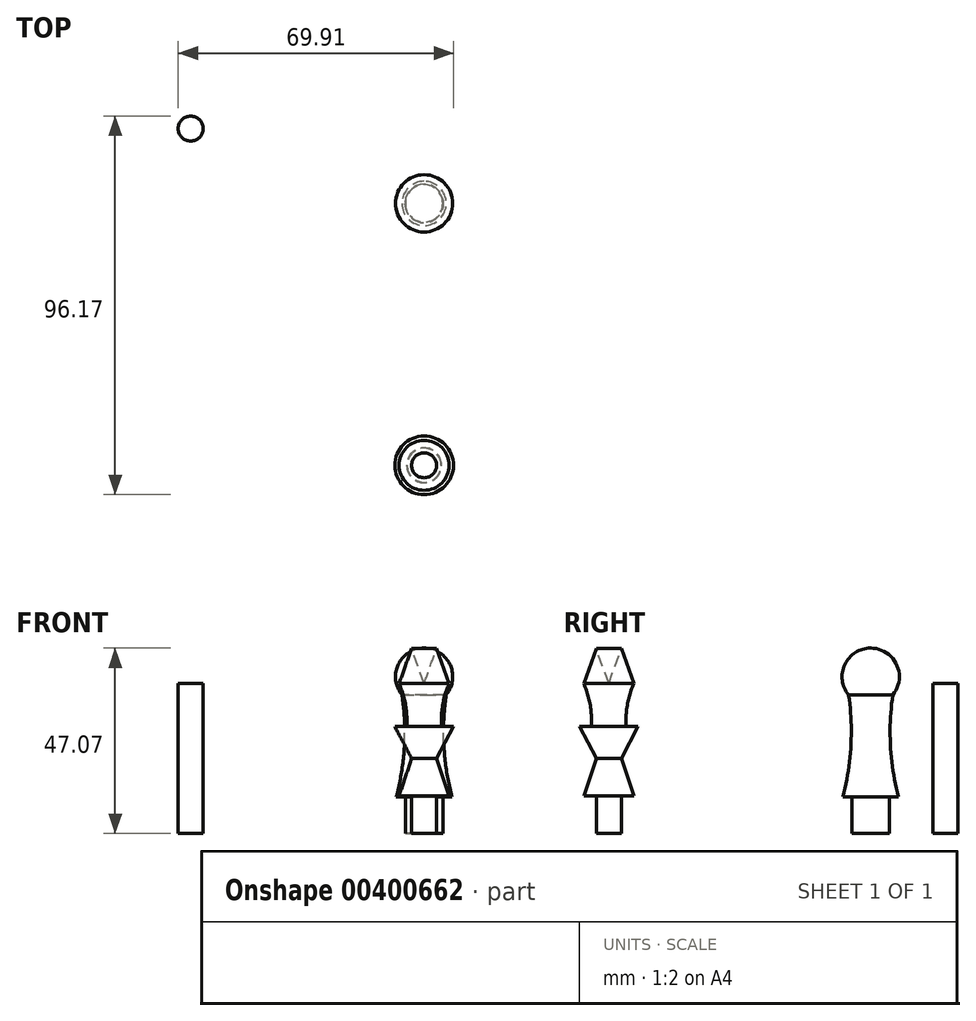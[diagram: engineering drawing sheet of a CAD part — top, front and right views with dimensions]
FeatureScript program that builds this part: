
annotation { "Feature Type Name" : "Feature", "Feature Type Description" : "" }
export const myFeature = defineFeature(function(context is Context, id is Id, definition is map)
    precondition{}
    {
        {
            var Q0;
            Q0=qCreatedBy(makeId("Top.planeOp"),FACE);
            var sketch = newSketch(context, id + "F0", { "sketchPlane" : qUnion([Q0])});
            skCircle(sketch, "E0", {"center": v(-59.29, 19) * mm, "radius": 3.18 * mm});
            skSolve(sketch);
        }
        {
            var Q0;
            Q0=makeQuery(id+"F0.imprint","IMPRINT",FACE,{"disambiguationData":[TD([[makeQuery(id+"F0.imprint","IMPRINT",EDGE,{"derivedFrom":sQuery(id+"F0.wireOp",EDGE,"E0")}),1.0]])]});
            extrude(context, id + "F1", {"entities" : qUnion([Q0]), "depth" : 38.1 * mm});
        }
        {
            var Q0;
            Q0=qCreatedBy(makeId("Right.planeOp"),FACE);
            var sketch = newSketch(context, id + "F2", { "sketchPlane" : qUnion([Q0])});
            skLineSegment(sketch, "E1", {"start": v(0, 0) * mm, "end": v(0, 47.07) * mm});
            skArc(sketch, "E2", {"start": v(5.62, 35.19) * mm, "mid": v(6.57, 42.9) * mm, "end": v(0, 47.07) * mm});
            skLineSegment(sketch, "E3", {"start": v(4.76, 0) * mm, "end": v(0, 0) * mm});
            skLineSegment(sketch, "E4", {"start": v(4.76, 0) * mm, "end": v(4.76, 9.26) * mm});
            skLineSegment(sketch, "E5", {"start": v(4.76, 9.26) * mm, "end": v(7.08, 9.26) * mm});
            skArc(sketch, "E6", {"start": v(5.62, 35.19) * mm, "mid": v(5.03, 22.15) * mm, "end": v(7.08, 9.26) * mm});
            skSolve(sketch);
        }
        {
            var Q0;
            Q0 = qSketchRegion(id + "F2", true);
            var Q1;
            Q1=sQuery(id+"F2.wireOp",EDGE,"E1");
            revolve(context, id + "F3", {"entities" : qUnion([Q0]), "axis" : qUnion([Q1]), "revolveType" : RevolveType.FULL});
        }
        {
            var Q0;
            Q0=qCreatedBy(makeId("Right.planeOp"),FACE);
            var sketch = newSketch(context, id + "F4", { "sketchPlane" : qUnion([Q0])});
            skLineSegment(sketch, "E7", {"start": v(-66.55, 0) * mm, "end": v(-63.37, 0) * mm});
            skLineSegment(sketch, "E8", {"start": v(-66.55, 0) * mm, "end": v(-66.55, 38.1) * mm});
            skArc(sketch, "E9", {"start": v(-60.2, 38.1) * mm, "mid": v(-61.8, 32.75) * mm, "end": v(-62.14, 27.18) * mm});
            skLineSegment(sketch, "E10", {"start": v(-66.55, 38.1) * mm, "end": v(-63.37, 46.99) * mm});
            skLineSegment(sketch, "E11", {"start": v(-63.37, 46.99) * mm, "end": v(-60.2, 38.1) * mm});
            skPoint(sketch, "E12.endSnap0", {"position": v(-60.2, 9.52) * mm});
            skLineSegment(sketch, "E13", {"start": v(-59.1, 27.18) * mm, "end": v(-62.14, 27.18) * mm});
            skPoint(sketch, "E14.start.orphan", {"position": v(-63.37, 0) * mm});
            skLineSegment(sketch, "E15", {"start": v(-63.37, 0) * mm, "end": v(-63.37, 9.52) * mm});
            skLineSegment(sketch, "E16", {"start": v(-63.37, 9.52) * mm, "end": v(-60.2, 9.52) * mm});
            skLineSegment(sketch, "E17", {"start": v(-60.2, 9.53) * mm, "end": v(-63.37, 19.05) * mm});
            skLineSegment(sketch, "E18", {"start": v(-63.37, 19.05) * mm, "end": v(-59.1, 27.18) * mm});
            skSolve(sketch);
        }
        {
            var Q0;
            Q0 = qSketchRegion(id + "F4", true);
            var Q1;
            Q1=sQuery(id+"F4.wireOp",EDGE,"E8");
            revolve(context, id + "F5", {"entities" : qUnion([Q0]), "axis" : qUnion([Q1]), "revolveType" : RevolveType.FULL});
        }
    });
